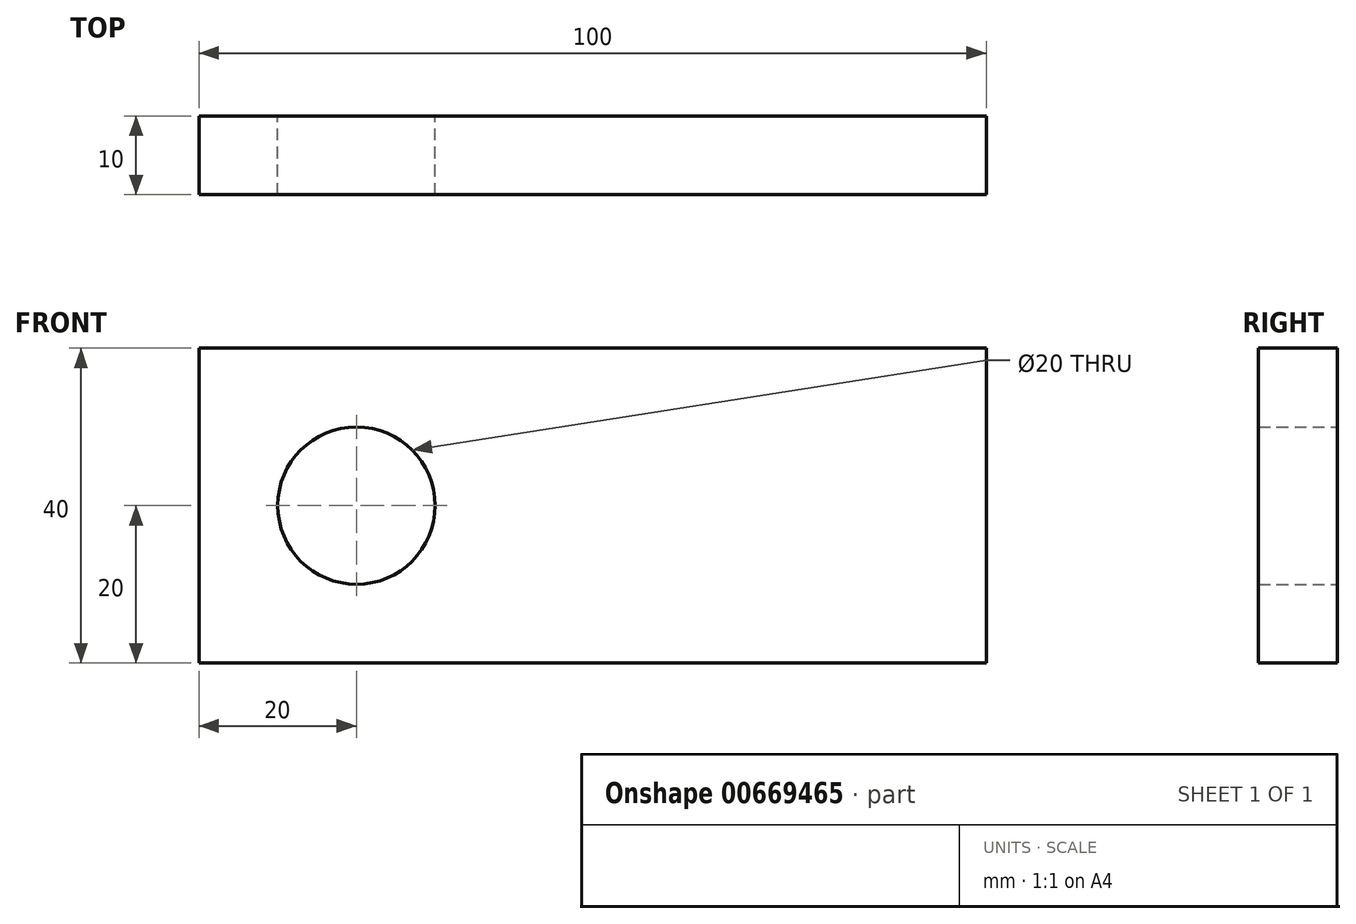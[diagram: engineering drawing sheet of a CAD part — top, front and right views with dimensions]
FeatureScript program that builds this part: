
annotation { "Feature Type Name" : "Feature", "Feature Type Description" : "" }
export const myFeature = defineFeature(function(context is Context, id is Id, definition is map)
    precondition{}
    {
        {
            var Q0;
            Q0=qCreatedBy(makeId("Front.planeOp"),FACE);
            var sketch = newSketch(context, id + "F0", { "sketchPlane" : qUnion([Q0])});
            skCircle(sketch, "E0", {"center": v(0, 0) * mm, "radius": 10 * mm});
            skLineSegment(sketch, "E1", {"start": v(-20, 0) * mm, "end": v(-20, -20) * mm});
            skLineSegment(sketch, "E2", {"start": v(-20, -20) * mm, "end": v(80, -20) * mm});
            skLineSegment(sketch, "E3", {"start": v(80, -20) * mm, "end": v(80, 20) * mm});
            skLineSegment(sketch, "E4", {"start": v(80, 20) * mm, "end": v(-20, 20) * mm});
            skLineSegment(sketch, "E5", {"start": v(-20, 20) * mm, "end": v(-20, 0) * mm});
            skSolve(sketch);
        }
        {
            var Q0;
            Q0=makeQuery(id+"F0.imprint","IMPRINT",FACE,{"disambiguationData":[TD([[makeQuery(id+"F0.imprint","IMPRINT",EDGE,{"derivedFrom":sQuery(id+"F0.wireOp",EDGE,"E0")}),-1.0]])]});
            extrude(context, id + "F1", {"entities" : qUnion([Q0]), "depth" : 10 * mm, "offsetDistance" : 25 * mm});
        }
    });
